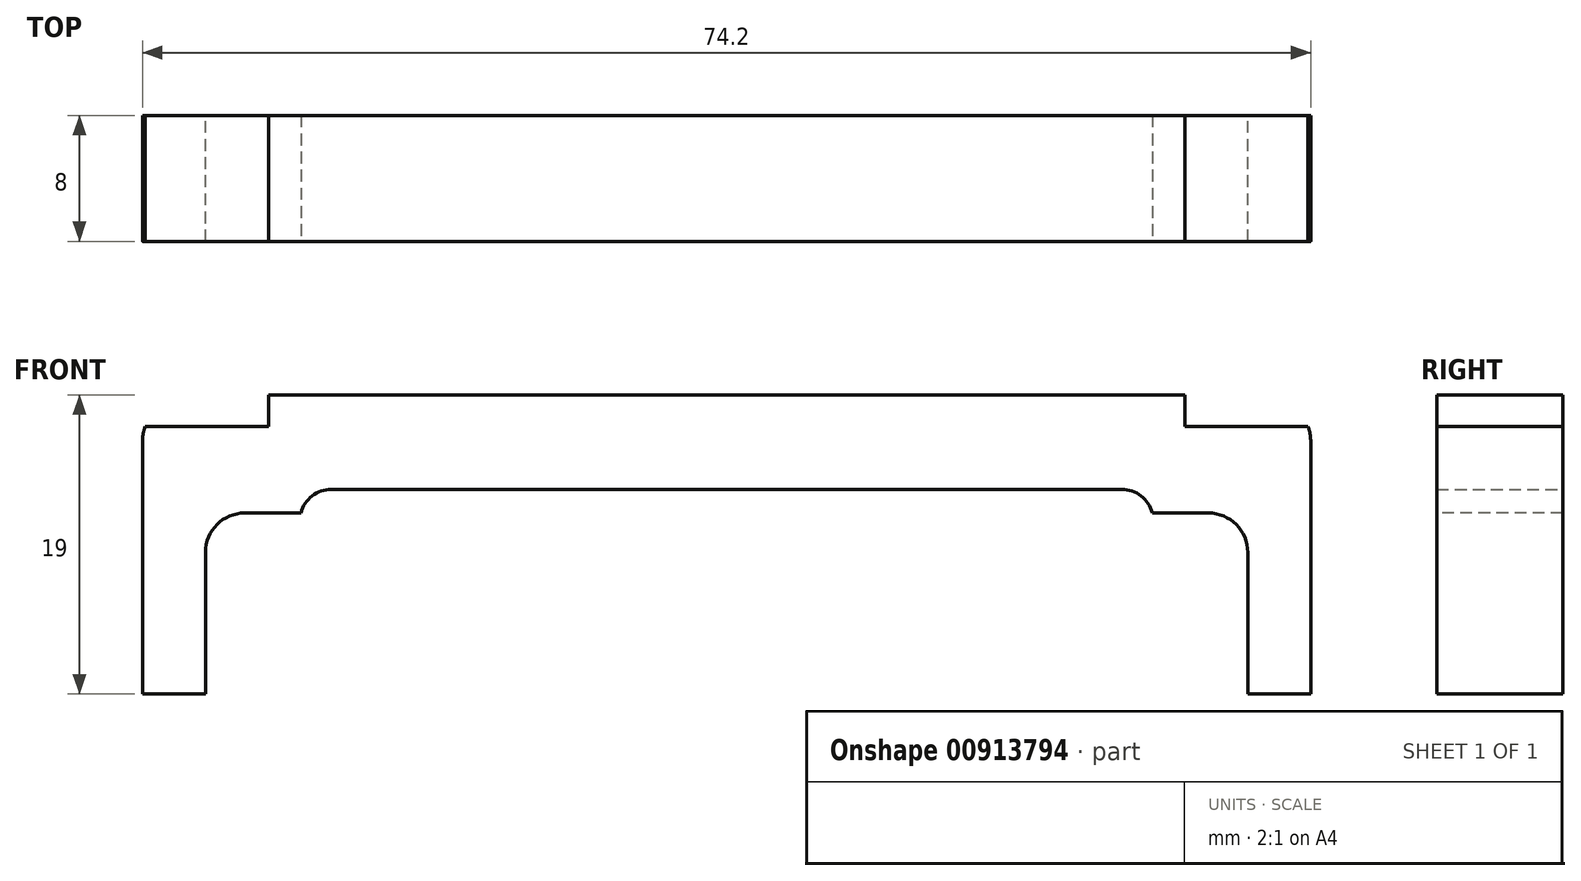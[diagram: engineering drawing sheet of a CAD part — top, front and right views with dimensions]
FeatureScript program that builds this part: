
annotation { "Feature Type Name" : "Feature", "Feature Type Description" : "" }
export const myFeature = defineFeature(function(context is Context, id is Id, definition is map)
    precondition{}
    {
        {
            var Q0;
            Q0=qCreatedBy(makeId("Front.planeOp"),FACE);
            var sketch = newSketch(context, id + "F0", { "sketchPlane" : qUnion([Q0])});
            skLineSegment(sketch, "E0.bottom", {"start": v(0, 0) * mm, "end": v(-37.1, 0) * mm});
            skLineSegment(sketch, "E0.top", {"start": v(0, 19) * mm, "end": v(-37.1, 19) * mm});
            skLineSegment(sketch, "E0.left", {"start": v(0, 0) * mm, "end": v(0, 19) * mm});
            skLineSegment(sketch, "E0.right", {"start": v(-37.1, 0) * mm, "end": v(-37.1, 19) * mm});
            skLineSegment(sketch, "E1.bottom", {"start": v(0, 0) * mm, "end": v(-27.1, 0) * mm});
            skLineSegment(sketch, "E1.top", {"start": v(0, 13) * mm, "end": v(-27.1, 13) * mm});
            skLineSegment(sketch, "E1.left", {"start": v(0, 0) * mm, "end": v(0, 13) * mm});
            skLineSegment(sketch, "E1.right", {"start": v(-27.1, 0) * mm, "end": v(-27.1, 13) * mm});
            skLineSegment(sketch, "E2.bottom", {"start": v(0, 0) * mm, "end": v(-33.1, 0) * mm});
            skLineSegment(sketch, "E2.top", {"start": v(0, 9) * mm, "end": v(-33.1, 9) * mm});
            skLineSegment(sketch, "E2.left", {"start": v(0, 0) * mm, "end": v(0, 9) * mm});
            skLineSegment(sketch, "E2.right", {"start": v(-33.1, 0) * mm, "end": v(-33.1, 9) * mm});
            skSolve(sketch);
        }
        {
            var Q0;
            {var subQ1=sQuery(id+"F0.wireOp",EDGE,"E0.top");Q0=makeQuery(id+"F0.imprint","IMPRINT",FACE,{"disambiguationData":[TD([[makeQuery(id+"F0.imprint","IMPRINT",EDGE,{"derivedFrom":subQ1}),1.0]])]});}
            extrude(context, id + "F1", {"entities" : qUnion([Q0]), "depth" : 8 * mm, "offsetDistance" : 25 * mm});
        }
        {
            var Q0;
            Q0=makeQuery(id+"FAmOGQda44bEUUD_1.opPattern","COPY",EDGE,{"derivedFrom":makeQuery(id+"F1.opExtrude","SWEPT_EDGE",EDGE,{"disambiguationData":[OSD([sQuery(id+"F0.wireOp",EDGE,"E1.top"),sQuery(id+"F0.wireOp",EDGE,"E1.right")])]}),"instanceName":"1"});
            var Q1;
            Q1=makeQuery(id+"F1.opExtrude","SWEPT_EDGE",EDGE,{"disambiguationData":[OSD([sQuery(id+"F0.wireOp",EDGE,"E1.top"),sQuery(id+"F0.wireOp",EDGE,"E1.right")])]});
            fillet(context, id + "F2", {"entities" : qUnion([Q0, Q1]), "radius" : 2 * mm, "tangentPropagation" : true, "allowEdgeOverflow" : false});
        }
        {
            var Q0;
            Q0=makeQuery(id+"F1.opExtrude","SWEPT_EDGE",EDGE,{"disambiguationData":[OSD([sQuery(id+"F0.wireOp",EDGE,"E0.top"),sQuery(id+"F0.wireOp",EDGE,"E0.right")])]});
            var Q1;
            Q1=makeQuery(id+"FAmOGQda44bEUUD_1.opPattern","COPY",EDGE,{"derivedFrom":makeQuery(id+"F1.opExtrude","SWEPT_EDGE",EDGE,{"disambiguationData":[OSD([sQuery(id+"F0.wireOp",EDGE,"E0.top"),sQuery(id+"F0.wireOp",EDGE,"E0.right")])]}),"instanceName":"1"});
            fillet(context, id + "F3", {"entities" : qUnion([Q0, Q1]), "radius" : 3 * mm, "tangentPropagation" : true, "allowEdgeOverflow" : false});
        }
        {
            var Q0;
            Q0=makeQuery(id+"F1.opExtrude","CAP_FACE",FACE,{"disambiguationData":[OSD([sQuery(id+"F0.wireOp",EDGE,"E0.bottom"),sQuery(id+"F0.wireOp",EDGE,"E0.top"),sQuery(id+"F0.wireOp",EDGE,"E0.left"),sQuery(id+"F0.wireOp",EDGE,"E0.right"),sQuery(id+"F0.wireOp",EDGE,"E1.top"),sQuery(id+"F0.wireOp",EDGE,"E1.right"),sQuery(id+"F0.wireOp",EDGE,"E2.top"),sQuery(id+"F0.wireOp",EDGE,"E2.right")])],"isStart":false});
            var sketch = newSketch(context, id + "F4", { "sketchPlane" : qUnion([Q0])});
            skPoint(sketch, "E3", {"position": v(-30.6, 9) * mm});
            skCircle(sketch, "E4", {"center": v(-30.6, 9) * mm, "radius": 2.5 * mm});
            skSolve(sketch);
        }
        {
            var Q0;
            Q0=qSketchRegion(id+"F4",true);
            extrude(context, id + "F5", {"entities" : qUnion([Q0]), "operationType" : NewBodyOperationType.REMOVE, "endBound" : BoundingType.THROUGH_ALL, "oppositeDirection" : true, "depth" : 25 * mm, "offsetDistance" : 25 * mm});
        }
        {
            var Q0;
            {var subQ7=sQuery(id+"F0.wireOp",EDGE,"E0.bottom");Q0=makeQuery(id+"F4.imprint","IMPRINT",FACE,{"disambiguationData":[TD([[makeQuery(id+"F4.imprint","IMPRINT",EDGE,{"derivedFrom":makeQuery(id+"F1.opExtrude","CAP_EDGE",EDGE,{"disambiguationData":[OSD([subQ7])],"isStart":false})}),-1.0]])]});}
            var sketch = newSketch(context, id + "F6", { "sketchPlane" : qUnion([Q0])});
            skLineSegment(sketch, "E5.bottom", {"start": v(-37.1, 19) * mm, "end": v(-29.1, 19) * mm});
            skLineSegment(sketch, "E5.top", {"start": v(-37.1, 17) * mm, "end": v(-29.1, 17) * mm});
            skLineSegment(sketch, "E5.left", {"start": v(-37.1, 19) * mm, "end": v(-37.1, 17) * mm});
            skLineSegment(sketch, "E5.right", {"start": v(-29.1, 19) * mm, "end": v(-29.1, 17) * mm});
            skLineSegment(sketch, "E6.bottom", {"start": v(-24.6, 11.5) * mm, "end": v(-30.6, 11.5) * mm});
            skLineSegment(sketch, "E6.top", {"start": v(-24.6, 8.5) * mm, "end": v(-30.6, 8.5) * mm});
            skLineSegment(sketch, "E6.left", {"start": v(-24.6, 11.5) * mm, "end": v(-24.6, 8.5) * mm});
            skLineSegment(sketch, "E6.right", {"start": v(-30.6, 11.5) * mm, "end": v(-30.6, 8.5) * mm});
            skSolve(sketch);
        }
        {
            var Q0;
            {var subQ5=sQuery(id+"F6.wireOp",EDGE,"E5.right");Q0=makeQuery(id+"F6.imprint","IMPRINT",FACE,{"disambiguationData":[TD([[makeQuery(id+"F6.imprint","IMPRINT",EDGE,{"derivedFrom":subQ5}),-1.0]])]});}
            var Q1;
            {var subQ0=sQuery(id+"F0.wireOp",EDGE,"E1.right");var subQ1=makeQuery(id+"F1.opExtrude","CAP_EDGE",EDGE,{"disambiguationData":[OSD([subQ0])],"isStart":false});var subQ14=makeQuery(id+"F4.imprint","IMPRINT",EDGE,{"derivedFrom":subQ1});Q1=makeQuery(id+"F6.imprint","IMPRINT",FACE,{"disambiguationData":[TD([[makeQuery(id+"F6.imprint","IMPRINT",EDGE,{"derivedFrom":subQ14}),1.0]])]});}
            extrude(context, id + "F7", {"entities" : qUnion([Q0, Q1]), "operationType" : NewBodyOperationType.REMOVE, "endBound" : BoundingType.THROUGH_ALL, "oppositeDirection" : true, "depth" : 25 * mm, "offsetDistance" : 25 * mm});
        }
        {
            var Q0;
            Q0=makeQuery(id+"F1.opExtrude","SWEPT_BODY",BODY,{"disambiguationData":[OSD([sQuery(id+"F0.wireOp",EDGE,"E0.bottom"),sQuery(id+"F0.wireOp",EDGE,"E0.top"),sQuery(id+"F0.wireOp",EDGE,"E0.left"),sQuery(id+"F0.wireOp",EDGE,"E0.right"),sQuery(id+"F0.wireOp",EDGE,"E1.top"),sQuery(id+"F0.wireOp",EDGE,"E1.right"),sQuery(id+"F0.wireOp",EDGE,"E2.top"),sQuery(id+"F0.wireOp",EDGE,"E2.right")])]});
            var Q1;
            Q1=qCreatedBy(makeId("Right.planeOp"),FACE);
            mirror(context, id + "F8", {"operationType" : NewBodyOperationType.ADD, "entities" : qUnion([Q0]), "mirrorPlane" : qUnion([Q1])});
        }
    });
